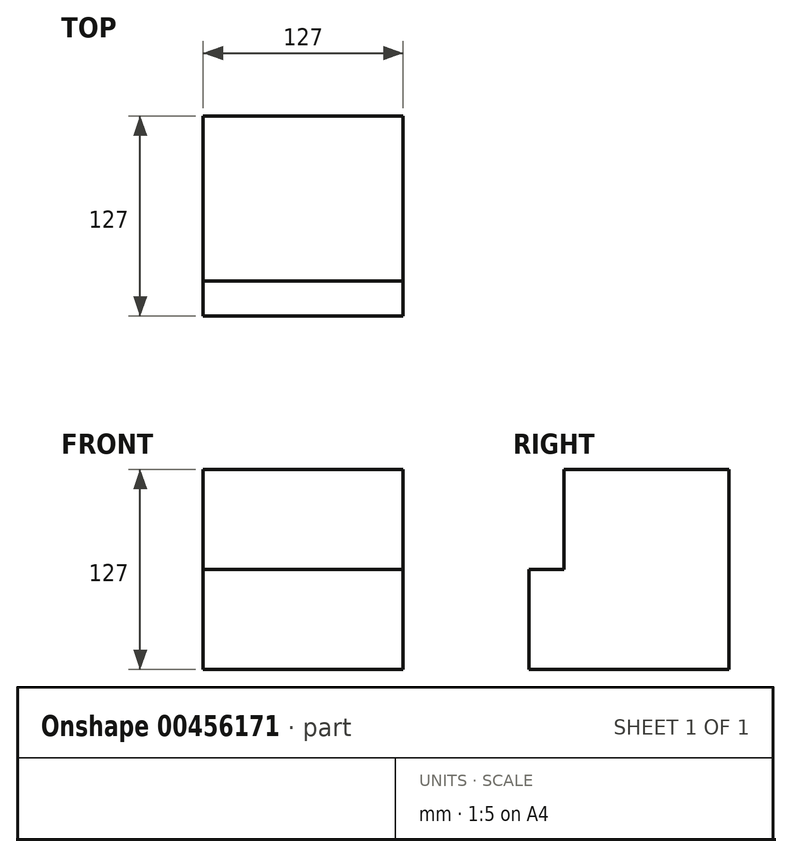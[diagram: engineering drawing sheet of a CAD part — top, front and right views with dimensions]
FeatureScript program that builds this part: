
annotation { "Feature Type Name" : "Feature", "Feature Type Description" : "" }
export const myFeature = defineFeature(function(context is Context, id is Id, definition is map)
    precondition{}
    {
        {
            var Q0;
            Q0=qCreatedBy(makeId("Front.planeOp"),FACE);
            var sketch = newSketch(context, id + "F0", { "sketchPlane" : qUnion([Q0])});
            skLineSegment(sketch, "E0.bottom", {"start": v(63.5, 63.5) * mm, "end": v(-63.5, 63.5) * mm});
            skLineSegment(sketch, "E0.top", {"start": v(63.5, -63.5) * mm, "end": v(-63.5, -63.5) * mm});
            skLineSegment(sketch, "E0.left", {"start": v(63.5, 63.5) * mm, "end": v(63.5, -63.5) * mm});
            skLineSegment(sketch, "E0.right", {"start": v(-63.5, 63.5) * mm, "end": v(-63.5, -63.5) * mm});
            skPoint(sketch, "E0.middle", {"position": v(0, 0) * mm});
            skSolve(sketch);
        }
        {
            var Q0;
            Q0 = qSketchRegion(id + "F0", true);
            extrude(context, id + "F1", {"entities" : qUnion([Q0]), "depth" : 63.5 * mm, "hasSecondDirection" : true, "secondDirectionOppositeDirection" : true, "secondDirectionDepth" : 63.5 * mm});
        }
        {
            var Q0;
            Q0=makeQuery(id+"F1.opExtrude","CAP_FACE",FACE,{"disambiguationData":[OSD([sQuery(id+"F0.wireOp",EDGE,"E0.bottom"),sQuery(id+"F0.wireOp",EDGE,"E0.top"),sQuery(id+"F0.wireOp",EDGE,"E0.left"),sQuery(id+"F0.wireOp",EDGE,"E0.right")])],"isStart":false});
            var sketch = newSketch(context, id + "F2", { "sketchPlane" : qUnion([Q0])});
            skLineSegment(sketch, "E1.bottom", {"start": v(-63.5, 63.5) * mm, "end": v(63.5, 63.5) * mm});
            skLineSegment(sketch, "E1.top", {"start": v(-63.5, 0) * mm, "end": v(63.5, 0) * mm});
            skLineSegment(sketch, "E1.left", {"start": v(-63.5, 63.5) * mm, "end": v(-63.5, 0) * mm});
            skLineSegment(sketch, "E1.right", {"start": v(63.5, 63.5) * mm, "end": v(63.5, 0) * mm});
            skSolve(sketch);
        }
        {
            var Q0;
            Q0=makeQuery(id+"F2.imprint","IMPRINT",FACE,{"disambiguationData":[TD([[makeQuery(id+"F2.imprint","IMPRINT",EDGE,{"derivedFrom":sQuery(id+"F2.wireOp",EDGE,"E1.bottom")}),1.0]])]});
            extrude(context, id + "F3", {"entities" : qUnion([Q0]), "operationType" : NewBodyOperationType.REMOVE, "endBound" : BoundingType.SYMMETRIC, "oppositeDirection" : true, "depth" : 44.45 * mm});
        }
    });
